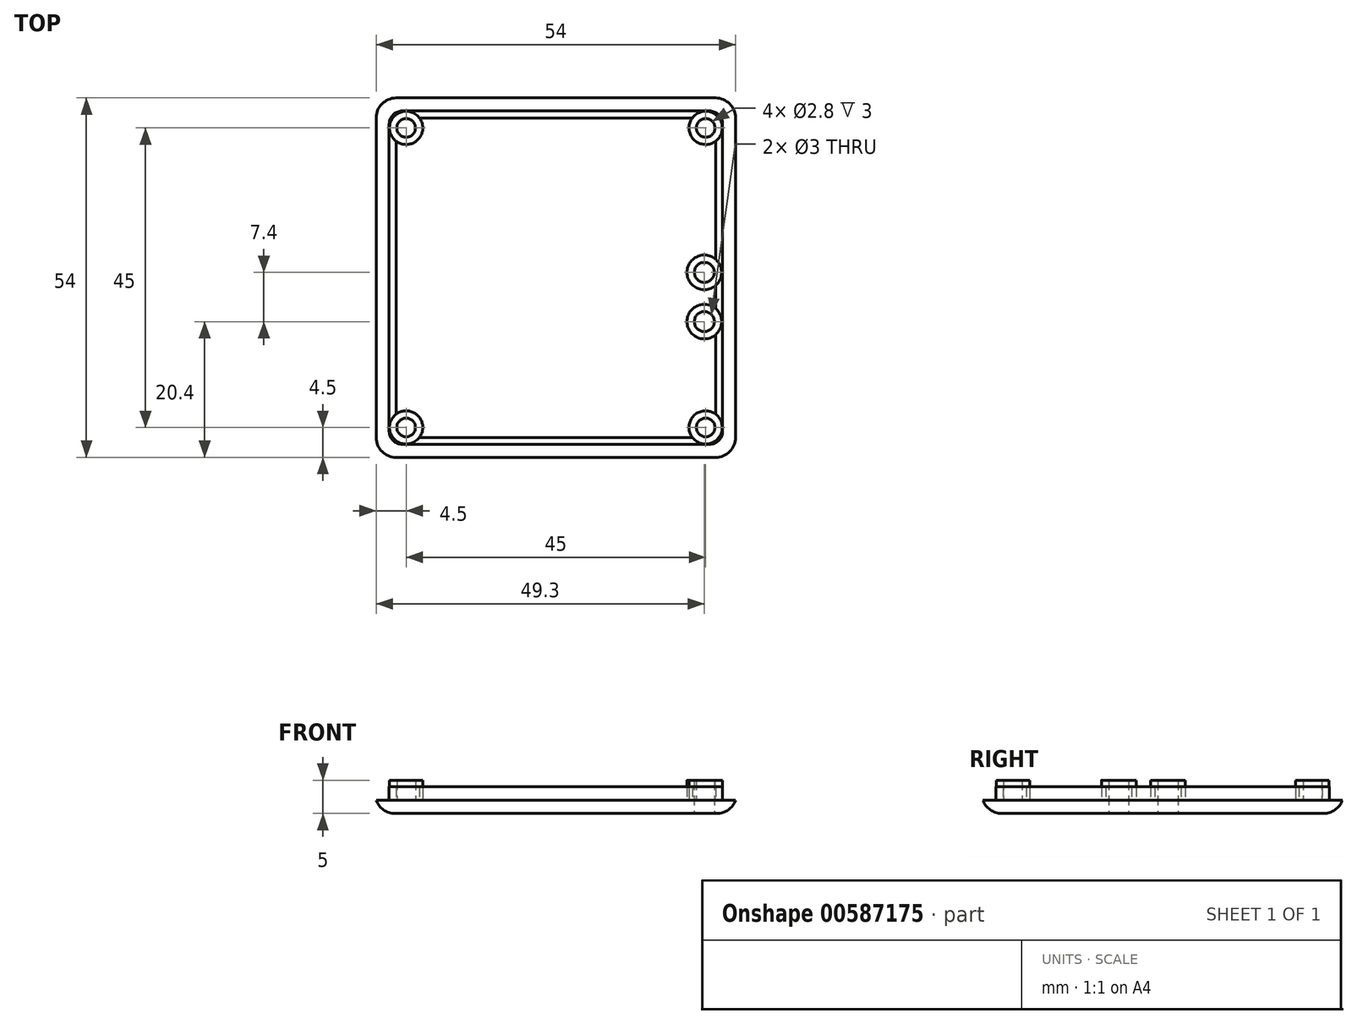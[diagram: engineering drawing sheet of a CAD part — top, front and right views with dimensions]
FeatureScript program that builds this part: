
annotation { "Feature Type Name" : "Feature", "Feature Type Description" : "" }
export const myFeature = defineFeature(function(context is Context, id is Id, definition is map)
    precondition{}
    {
        {
            var Q0;
            Q0=qCreatedBy(makeId("Top.planeOp"),FACE);
            var sketch = newSketch(context, id + "F0", { "sketchPlane" : qUnion([Q0])});
            skLineSegment(sketch, "E0.bottom", {"start": v(-27, 27) * mm, "end": v(27, 27) * mm});
            skLineSegment(sketch, "E0.top", {"start": v(-27, -27) * mm, "end": v(27, -27) * mm});
            skLineSegment(sketch, "E0.left", {"start": v(-27, 27) * mm, "end": v(-27, -27) * mm});
            skLineSegment(sketch, "E0.right", {"start": v(27, 27) * mm, "end": v(27, -27) * mm});
            skSolve(sketch);
        }
        {
            var Q0;
            Q0 = qSketchRegion(id + "F0", true);
            extrude(context, id + "F1", {"entities" : qUnion([Q0]), "depth" : 2 * mm, "offsetDistance" : 25 * mm});
        }
        {
            var Q0;
            Q0=makeQuery(id+"F1.opExtrude","SWEPT_EDGE",EDGE,{"disambiguationData":[OSD([sQuery(id+"F0.wireOp",EDGE,"E0.top"),sQuery(id+"F0.wireOp",EDGE,"E0.left")])]});
            var Q1;
            Q1=makeQuery(id+"F1.opExtrude","SWEPT_EDGE",EDGE,{"disambiguationData":[OSD([sQuery(id+"F0.wireOp",EDGE,"E0.bottom"),sQuery(id+"F0.wireOp",EDGE,"E0.left")])]});
            var Q2;
            Q2=makeQuery(id+"F1.opExtrude","SWEPT_EDGE",EDGE,{"disambiguationData":[OSD([sQuery(id+"F0.wireOp",EDGE,"E0.bottom"),sQuery(id+"F0.wireOp",EDGE,"E0.right")])]});
            var Q3;
            Q3=makeQuery(id+"F1.opExtrude","SWEPT_EDGE",EDGE,{"disambiguationData":[OSD([sQuery(id+"F0.wireOp",EDGE,"E0.top"),sQuery(id+"F0.wireOp",EDGE,"E0.right")])]});
            fillet(context, id + "F2", {"entities" : qUnion([Q0, Q1, Q2, Q3]), "radius" : 3 * mm, "tangentPropagation" : true, "allowEdgeOverflow" : false});
        }
        {
            var Q0;
            Q0=makeQuery(id+"F1.opExtrude","CAP_FACE",FACE,{"disambiguationData":[OSD([sQuery(id+"F0.wireOp",EDGE,"E0.bottom"),sQuery(id+"F0.wireOp",EDGE,"E0.top"),sQuery(id+"F0.wireOp",EDGE,"E0.left"),sQuery(id+"F0.wireOp",EDGE,"E0.right")])],"isStart":true});
            fillet(context, id + "F3", {"entities" : qUnion([Q0]), "radius" : 3 * mm, "tangentPropagation" : true, "allowEdgeOverflow" : false});
        }
        {
            var Q0;
            Q0=makeQuery(id+"F1.opExtrude","CAP_FACE",FACE,{"disambiguationData":[OSD([sQuery(id+"F0.wireOp",EDGE,"E0.bottom"),sQuery(id+"F0.wireOp",EDGE,"E0.top"),sQuery(id+"F0.wireOp",EDGE,"E0.left"),sQuery(id+"F0.wireOp",EDGE,"E0.right")])],"isStart":false});
            var sketch = newSketch(context, id + "F4", { "sketchPlane" : qUnion([Q0])});
            skLineSegment(sketch, "E1.bottom", {"start": v(-25.05, 25.05) * mm, "end": v(25.05, 25.05) * mm});
            skLineSegment(sketch, "E1.top", {"start": v(-25.05, -25.05) * mm, "end": v(25.05, -25.05) * mm});
            skLineSegment(sketch, "E1.left", {"start": v(-25.05, 25.05) * mm, "end": v(-25.05, -25.05) * mm});
            skLineSegment(sketch, "E1.right", {"start": v(25.05, 25.05) * mm, "end": v(25.05, -25.05) * mm});
            skLineSegment(sketch, "E2.bottom", {"start": v(-24, 24) * mm, "end": v(24, 24) * mm});
            skLineSegment(sketch, "E2.top", {"start": v(-24, -24) * mm, "end": v(24, -24) * mm});
            skLineSegment(sketch, "E2.left", {"start": v(-24, 24) * mm, "end": v(-24, -24) * mm});
            skLineSegment(sketch, "E2.right", {"start": v(24, 24) * mm, "end": v(24, -24) * mm});
            skSolve(sketch);
        }
        {
            var Q0;
            Q0 = qSketchRegion(id + "F4", true);
            extrude(context, id + "F5", {"entities" : qUnion([Q0]), "operationType" : NewBodyOperationType.ADD, "depth" : 2 * mm, "offsetDistance" : 25 * mm});
        }
        {
            var Q0;
            Q0=makeQuery(id+"F5.boolean.opBoolean","SPLIT",FACE,{"disambiguationData":[TD([makeQuery(id+"F5.opExtrude","SWEPT_FACE",FACE,{"disambiguationData":[OSD([sQuery(id+"F4.wireOp",EDGE,"E2.bottom")])]})])],"derivedFrom":makeQuery(id+"F1.opExtrude","CAP_FACE",FACE,{"disambiguationData":[OSD([sQuery(id+"F0.wireOp",EDGE,"E0.bottom"),sQuery(id+"F0.wireOp",EDGE,"E0.top"),sQuery(id+"F0.wireOp",EDGE,"E0.left"),sQuery(id+"F0.wireOp",EDGE,"E0.right")])],"isStart":false})});
            var sketch = newSketch(context, id + "F6", { "sketchPlane" : qUnion([Q0])});
            skLineSegment(sketch, "E3.bottom", {"start": v(-22.5, 22.5) * mm, "end": v(22.5, 22.5) * mm, "construction": true});
            skLineSegment(sketch, "E3.top", {"start": v(-22.5, -22.5) * mm, "end": v(22.5, -22.5) * mm, "construction": true});
            skLineSegment(sketch, "E3.left", {"start": v(-22.5, 22.5) * mm, "end": v(-22.5, -22.5) * mm, "construction": true});
            skLineSegment(sketch, "E3.right", {"start": v(22.5, 22.5) * mm, "end": v(22.5, -22.5) * mm, "construction": true});
            skCircle(sketch, "E4", {"center": v(-22.5, 22.5) * mm, "radius": 2.5 * mm});
            skCircle(sketch, "E5", {"center": v(22.5, 22.5) * mm, "radius": 2.5 * mm});
            skCircle(sketch, "E6", {"center": v(22.5, -22.5) * mm, "radius": 2.5 * mm});
            skCircle(sketch, "E7", {"center": v(-22.5, -22.5) * mm, "radius": 2.5 * mm});
            skCircle(sketch, "E8", {"center": v(-22.5, 22.5) * mm, "radius": 1.4 * mm});
            skCircle(sketch, "E9", {"center": v(22.5, 22.5) * mm, "radius": 1.4 * mm});
            skCircle(sketch, "E10", {"center": v(-22.5, -22.5) * mm, "radius": 1.4 * mm});
            skCircle(sketch, "E11", {"center": v(22.5, -22.5) * mm, "radius": 1.4 * mm});
            skSolve(sketch);
        }
        {
            var Q0;
            Q0 = qSketchRegion(id + "F6", true);
            extrude(context, id + "F7", {"entities" : qUnion([Q0]), "operationType" : NewBodyOperationType.ADD, "depth" : 3 * mm, "offsetDistance" : 25 * mm});
        }
        {
            var Q0;
            Q0=makeQuery(id+"F5.opExtrude","SWEPT_EDGE",EDGE,{"disambiguationData":[OSD([sQuery(id+"F4.wireOp",EDGE,"E1.top"),sQuery(id+"F4.wireOp",EDGE,"E1.left")])]});
            var Q1;
            Q1=makeQuery(id+"F5.opExtrude","SWEPT_EDGE",EDGE,{"disambiguationData":[OSD([sQuery(id+"F4.wireOp",EDGE,"E1.top"),sQuery(id+"F4.wireOp",EDGE,"E1.right")])]});
            var Q2;
            Q2=makeQuery(id+"F5.opExtrude","SWEPT_EDGE",EDGE,{"disambiguationData":[OSD([sQuery(id+"F4.wireOp",EDGE,"E1.bottom"),sQuery(id+"F4.wireOp",EDGE,"E1.right")])]});
            var Q3;
            Q3=makeQuery(id+"F5.opExtrude","SWEPT_EDGE",EDGE,{"disambiguationData":[OSD([sQuery(id+"F4.wireOp",EDGE,"E1.bottom"),sQuery(id+"F4.wireOp",EDGE,"E1.left")])]});
            fillet(context, id + "F8", {"entities" : qUnion([Q0, Q1, Q2, Q3]), "radius" : 2 * mm, "tangentPropagation" : true, "allowEdgeOverflow" : false});
        }
        {
            var Q0;
            {var subQ3=makeQuery(id+"F5.opExtrude","SWEPT_FACE",FACE,{"disambiguationData":[OSD([sQuery(id+"F4.wireOp",EDGE,"E2.bottom")])]});Q0=makeQuery(id+"F7.boolean.opBoolean","SPLIT",FACE,{"disambiguationData":[TD([subQ3])],"derivedFrom":makeQuery(id+"F5.boolean.opBoolean","SPLIT",FACE,{"disambiguationData":[TD([subQ3])],"derivedFrom":makeQuery(id+"F1.opExtrude","CAP_FACE",FACE,{"disambiguationData":[OSD([sQuery(id+"F0.wireOp",EDGE,"E0.bottom"),sQuery(id+"F0.wireOp",EDGE,"E0.top"),sQuery(id+"F0.wireOp",EDGE,"E0.left"),sQuery(id+"F0.wireOp",EDGE,"E0.right")])],"isStart":false})})});}
            var sketch = newSketch(context, id + "F9", { "sketchPlane" : qUnion([Q0])});
            skCircle(sketch, "E12", {"center": v(22.3, 0.8) * mm, "radius": 1.5 * mm});
            skCircle(sketch, "E13", {"center": v(22.3, -6.6) * mm, "radius": 1.5 * mm});
            skCircle(sketch, "E14", {"center": v(22.3, 0.8) * mm, "radius": 2.6 * mm});
            skCircle(sketch, "E15", {"center": v(22.3, -6.6) * mm, "radius": 2.6 * mm});
            skSolve(sketch);
        }
        {
            var Q0;
            Q0 = qSketchRegion(id + "F9", true);
            extrude(context, id + "F10", {"entities" : qUnion([Q0]), "operationType" : NewBodyOperationType.ADD, "depth" : 3 * mm, "offsetDistance" : 25 * mm});
        }
        {
            var Q0;
            {var subQ4=makeQuery(id+"F5.opExtrude","SWEPT_FACE",FACE,{"disambiguationData":[OSD([sQuery(id+"F4.wireOp",EDGE,"E2.bottom")])]});Q0=makeQuery(id+"F10.boolean.opBoolean","SPLIT",FACE,{"disambiguationData":[TD([subQ4])],"derivedFrom":makeQuery(id+"F7.boolean.opBoolean","SPLIT",FACE,{"disambiguationData":[TD([subQ4])],"derivedFrom":makeQuery(id+"F5.boolean.opBoolean","SPLIT",FACE,{"disambiguationData":[TD([subQ4])],"derivedFrom":makeQuery(id+"F1.opExtrude","CAP_FACE",FACE,{"disambiguationData":[OSD([sQuery(id+"F0.wireOp",EDGE,"E0.bottom"),sQuery(id+"F0.wireOp",EDGE,"E0.top"),sQuery(id+"F0.wireOp",EDGE,"E0.left"),sQuery(id+"F0.wireOp",EDGE,"E0.right")])],"isStart":false})})})});}
            var sketch = newSketch(context, id + "F11", { "sketchPlane" : qUnion([Q0])});
            skCircle(sketch, "E16", {"center": v(22.3, 0.8) * mm, "radius": 1.5 * mm});
            skCircle(sketch, "E17", {"center": v(22.3, -6.6) * mm, "radius": 1.5 * mm});
            skSolve(sketch);
        }
        {
            var Q0;
            Q0 = qSketchRegion(id + "F11", true);
            extrude(context, id + "F12", {"entities" : qUnion([Q0]), "operationType" : NewBodyOperationType.REMOVE, "oppositeDirection" : true, "depth" : 25 * mm, "offsetDistance" : 25 * mm});
        }
    });
